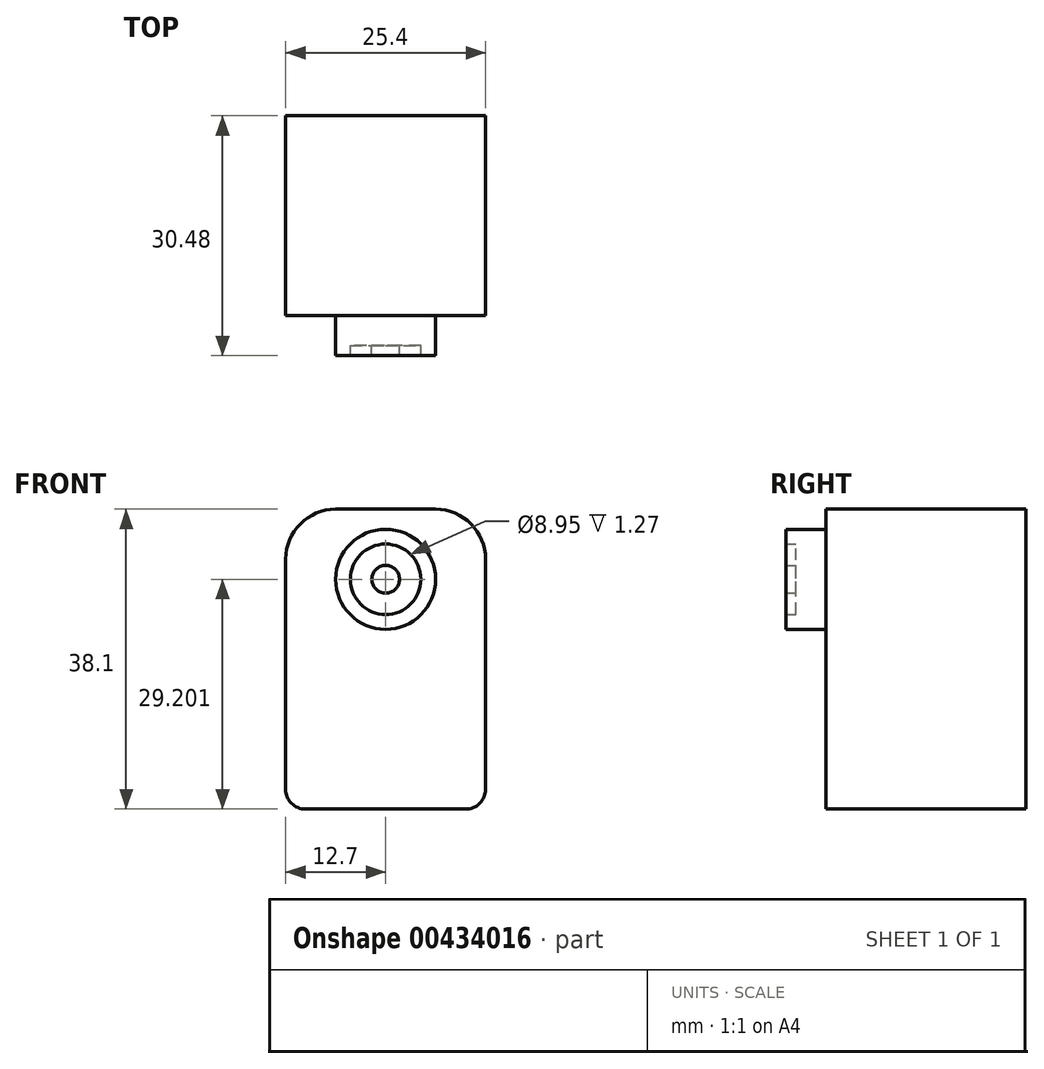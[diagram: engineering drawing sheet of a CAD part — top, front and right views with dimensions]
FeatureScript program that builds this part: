
annotation { "Feature Type Name" : "Feature", "Feature Type Description" : "" }
export const myFeature = defineFeature(function(context is Context, id is Id, definition is map)
    precondition{}
    {
        {
            var Q0;
            Q0=qCreatedBy(makeId("Front.planeOp"),FACE);
            var sketch = newSketch(context, id + "F0", { "sketchPlane" : qUnion([Q0])});
            skLineSegment(sketch, "E0", {"start": v(0, 2.54) * mm, "end": v(0, 31.75) * mm});
            skLineSegment(sketch, "E1", {"start": v(6.35, 38.1) * mm, "end": v(19.05, 38.1) * mm});
            skLineSegment(sketch, "E2", {"start": v(25.4, 31.75) * mm, "end": v(25.4, 2.54) * mm});
            skLineSegment(sketch, "E3", {"start": v(22.86, 0) * mm, "end": v(2.54, 0) * mm});
            skPoint(sketch, "E4.visualSharp", {"position": v(0, 38.1) * mm});
            skArc(sketch, "E4.filletArc", {"start": v(6.35, 38.1) * mm, "mid": v(1.86, 36.24) * mm, "end": v(0, 31.75) * mm});
            skPoint(sketch, "E5.visualSharp", {"position": v(25.4, 38.1) * mm});
            skArc(sketch, "E5.filletArc", {"start": v(25.4, 31.75) * mm, "mid": v(23.54, 36.24) * mm, "end": v(19.05, 38.1) * mm});
            skPoint(sketch, "E6.visualSharp", {"position": v(25.4, 0) * mm});
            skArc(sketch, "E6.filletArc", {"start": v(22.86, 0) * mm, "mid": v(24.66, 0.74) * mm, "end": v(25.4, 2.54) * mm});
            skPoint(sketch, "E7.visualSharp", {"position": v(0, 0) * mm});
            skArc(sketch, "E7.filletArc", {"start": v(0, 2.54) * mm, "mid": v(0.74, 0.74) * mm, "end": v(2.54, 0) * mm});
            skSolve(sketch);
        }
        {
            var Q0;
            Q0 = qSketchRegion(id + "F0", true);
            extrude(context, id + "F1", {"entities" : qUnion([Q0]), "oppositeDirection" : true, "depth" : 25.4 * mm});
        }
        {
            var Q0;
            Q0=makeQuery(id+"F1.opExtrude","CAP_FACE",FACE,{"disambiguationData":[OSD([sQuery(id+"F0.wireOp",EDGE,"E0"),sQuery(id+"F0.wireOp",EDGE,"E1"),sQuery(id+"F0.wireOp",EDGE,"E2"),sQuery(id+"F0.wireOp",EDGE,"E3"),sQuery(id+"F0.wireOp",EDGE,"E4.filletArc"),sQuery(id+"F0.wireOp",EDGE,"E5.filletArc"),sQuery(id+"F0.wireOp",EDGE,"E6.filletArc"),sQuery(id+"F0.wireOp",EDGE,"E7.filletArc")])],"isStart":true});
            var sketch = newSketch(context, id + "F2", { "sketchPlane" : qUnion([Q0])});
            skCircle(sketch, "E8", {"center": v(12.7, 29.2) * mm, "radius": 6.35 * mm});
            skPoint(sketch, "E8.centerSnap0", {"position": v(12.7, 38.1) * mm});
            skCircle(sketch, "E9", {"center": v(12.7, 29.2) * mm, "radius": 4.48 * mm});
            skSolve(sketch);
        }
        {
            var Q0;
            Q0=makeQuery(id+"F2.imprint","IMPRINT",FACE,{"disambiguationData":[TD([[makeQuery(id+"F2.imprint","IMPRINT",EDGE,{"derivedFrom":sQuery(id+"F2.wireOp",EDGE,"E8")}),1.0]])]});
            extrude(context, id + "F3", {"entities" : qUnion([Q0]), "operationType" : NewBodyOperationType.ADD, "depth" : 5.08 * mm});
        }
        {
            var Q0;
            Q0=makeQuery(id+"F3.boolean.opBoolean","SPLIT",FACE,{"disambiguationData":[TD([makeQuery(id+"F3.opExtrude","SWEPT_FACE",FACE,{"disambiguationData":[OSD([sQuery(id+"F2.wireOp",EDGE,"E9")])]})])],"derivedFrom":makeQuery(id+"F1.opExtrude","CAP_FACE",FACE,{"disambiguationData":[OSD([sQuery(id+"F0.wireOp",EDGE,"E0"),sQuery(id+"F0.wireOp",EDGE,"E1"),sQuery(id+"F0.wireOp",EDGE,"E2"),sQuery(id+"F0.wireOp",EDGE,"E3"),sQuery(id+"F0.wireOp",EDGE,"E4.filletArc"),sQuery(id+"F0.wireOp",EDGE,"E5.filletArc"),sQuery(id+"F0.wireOp",EDGE,"E6.filletArc"),sQuery(id+"F0.wireOp",EDGE,"E7.filletArc")])],"isStart":true})});
            extrude(context, id + "F4", {"entities" : qUnion([Q0]), "operationType" : NewBodyOperationType.ADD, "depth" : 3.8 * mm});
        }
        {
            var Q0;
            Q0=makeQuery(id+"F4.opExtrude","CAP_FACE",FACE,{"disambiguationData":[OSD([sQuery(id+"F0.wireOp",EDGE,"E0"),sQuery(id+"F0.wireOp",EDGE,"E1"),sQuery(id+"F0.wireOp",EDGE,"E2"),sQuery(id+"F0.wireOp",EDGE,"E3"),sQuery(id+"F0.wireOp",EDGE,"E4.filletArc"),sQuery(id+"F0.wireOp",EDGE,"E5.filletArc"),sQuery(id+"F0.wireOp",EDGE,"E6.filletArc"),sQuery(id+"F0.wireOp",EDGE,"E7.filletArc")])],"isStart":false});
            var sketch = newSketch(context, id + "F5", { "sketchPlane" : qUnion([Q0])});
            skCircle(sketch, "E10", {"center": v(12.7, 29.2) * mm, "radius": 1.76 * mm});
            skSolve(sketch);
        }
        {
            var Q0;
            Q0 = qSketchRegion(id + "F5", true);
            extrude(context, id + "F6", {"entities" : qUnion([Q0]), "depth" : 1.27 * mm});
        }
    });
